# Revit family: VK-AF
name_source: partatom
category: Duct Accessories
units: mm (PartAtom-declared; Revit-internal decimal feet)

## family parameters
Always vertical = Yes
Cut with Voids When Loaded = No
Part Type = Attaches To
Round Connector Dimension = Use Diameter
Shared = No
Work Plane-Based = No

## types (11) — shared parameters
00_20_Manufacturer = BLAUBERG
00_20_Name = Inlet cone
Casing Material = Metal, painted, grey, matt RAL 7040
Dn = 905 mm
Dy = 900 mm
Load Classification = HVAC
Maintenance zone material = <By Category>
Manufacturer = BLAUBERG
zero-valued in all types: Default Elevation

## per-type parameters (varying)
| type | D | D1 | D2 | Diameter | F | F1 | F2 | H | Length | R | R1 | R2 | Weight | d | f | f1 | f2 | n |
| VK-AF-400 | 400 mm  [stored 1.31234 ft] | 450 mm  [stored 1.47638 ft] | 490 mm  [stored 1.60761 ft] | 540 mm  [stored 1.77165 ft] | 450 mm  [stored 1.47638 ft] | 500 mm  [stored 1.64042 ft] | 540 mm  [stored 1.77165 ft] | 95 mm | 95 mm | 200 mm  [stored 0.656168 ft] | 225 mm  [stored 0.738189 ft] | 245 mm  [stored 0.803806 ft] | 2.70 kg | 8 mm  [stored 0.0262467 ft] | 225 mm  [stored 0.738189 ft] | 250 mm  [stored 0.82021 ft] | 270 mm  [stored 0.885827 ft] | 12 |
| VK-AF-1250 | 1250 mm | 1320 mm | 1400 mm | 1550 mm | 1400 mm | 1470 mm | 1550 mm | 285 mm  [stored 0.935039 ft] | 285 mm  [stored 0.935039 ft] | 625 mm | 660 mm | 700 mm | 53.50 kg | 15 mm  [stored 0.0492126 ft] | 700 mm | 735 mm | 775 mm | 20 |
| VK-AF-450 | 450 mm  [stored 1.47638 ft] | 500 mm  [stored 1.64042 ft] | 540 mm  [stored 1.77165 ft] | 600 mm | 500 mm  [stored 1.64042 ft] | 560 mm | 600 mm | 110 mm  [stored 0.360892 ft] | 110 mm  [stored 0.360892 ft] | 225 mm  [stored 0.738189 ft] | 250 mm  [stored 0.82021 ft] | 270 mm  [stored 0.885827 ft] | 3.30 kg | 8 mm  [stored 0.0262467 ft] | 250 mm  [stored 0.82021 ft] | 280 mm  [stored 0.918635 ft] | 300 mm | 12 |
| VK-AF-500 | 500 mm  [stored 1.64042 ft] | 560 mm | 600 mm | 660 mm | 560 mm | 620 mm | 660 mm | 120 mm  [stored 0.393701 ft] | 120 mm  [stored 0.393701 ft] | 250 mm  [stored 0.82021 ft] | 280 mm  [stored 0.918635 ft] | 300 mm | 4.00 kg | 12 mm  [stored 0.0393701 ft] | 280 mm  [stored 0.918635 ft] | 310 mm  [stored 1.01706 ft] | 330 mm | 12 |
| VK-AF-560 | 560 mm | 620 mm | 660 mm | 730 mm | 630 mm | 690 mm | 730 mm | 135 mm  [stored 0.442913 ft] | 135 mm  [stored 0.442913 ft] | 280 mm  [stored 0.918635 ft] | 310 mm  [stored 1.01706 ft] | 330 mm | 4.65 kg | 12 mm  [stored 0.0393701 ft] | 315 mm  [stored 1.03346 ft] | 345 mm  [stored 1.13189 ft] | 365 mm  [stored 1.19751 ft] | 12 |
| VK-AF-630 | 630 mm | 690 mm | 730 mm | 810 mm | 710 mm | 770 mm | 810 mm | 150 mm | 150 mm | 315 mm  [stored 1.03346 ft] | 345 mm  [stored 1.13189 ft] | 365 mm  [stored 1.19751 ft] | 6.80 kg | 12 mm  [stored 0.0393701 ft] | 355 mm | 385 mm  [stored 1.26312 ft] | 405 mm | 12 |
| VK-AF-710 | 710 mm | 770 mm | 810 mm | 900 mm | 800 mm | 860 mm | 900 mm | 170 mm  [stored 0.557743 ft] | 170 mm  [stored 0.557743 ft] | 355 mm | 385 mm  [stored 1.26312 ft] | 405 mm | 12.00 kg | 12 mm  [stored 0.0393701 ft] | 400 mm  [stored 1.31234 ft] | 430 mm | 450 mm  [stored 1.47638 ft] | 16 |
| VK-AF-800 | 800 mm | 860 mm | 900 mm | 1015 mm | 900 mm | 970 mm | 1015 mm | 190 mm | 190 mm | 400 mm  [stored 1.31234 ft] | 430 mm | 450 mm  [stored 1.47638 ft] | 15.00 kg | 12 mm  [stored 0.0393701 ft] | 450 mm  [stored 1.47638 ft] | 485 mm  [stored 1.59121 ft] | 508 mm | 16 |
| VK-AF-900 | 900 mm | 970 mm | 1015 mm | 1115 mm | 1000 mm | 1070 mm | 1115 mm | 210 mm  [stored 0.688976 ft] | 210 mm  [stored 0.688976 ft] | 450 mm  [stored 1.47638 ft] | 485 mm  [stored 1.59121 ft] | 508 mm | 21.00 kg | 15 mm  [stored 0.0492126 ft] | 500 mm  [stored 1.64042 ft] | 535 mm  [stored 1.75525 ft] | 558 mm | 16 |
| VK-AF-1000 | 1000 mm | 1070 mm | 1115 mm | 1270 mm | 1120 mm | 1190 mm | 1270 mm | 240 mm  [stored 0.787402 ft] | 240 mm  [stored 0.787402 ft] | 500 mm  [stored 1.64042 ft] | 535 mm  [stored 1.75525 ft] | 558 mm | 36.70 kg | 15 mm  [stored 0.0492126 ft] | 560 mm | 595 mm | 635 mm | 16 |
| VK-AF-1120 | 1120 mm | 1190 mm | 1270 mm | 1400 mm | 1250 mm | 1320 mm | 1400 mm | 255 mm  [stored 0.836614 ft] | 255 mm  [stored 0.836614 ft] | 560 mm | 595 mm | 635 mm | 45.00 kg | 15 mm  [stored 0.0492126 ft] | 625 mm | 660 mm | 700 mm | 20 |

note: column(s) folded — value = type name in every type: 00_20_Type

note: [stored X ft] marks values corroborated as IEEE doubles in the binary element streams (Revit-internal decimal feet)
